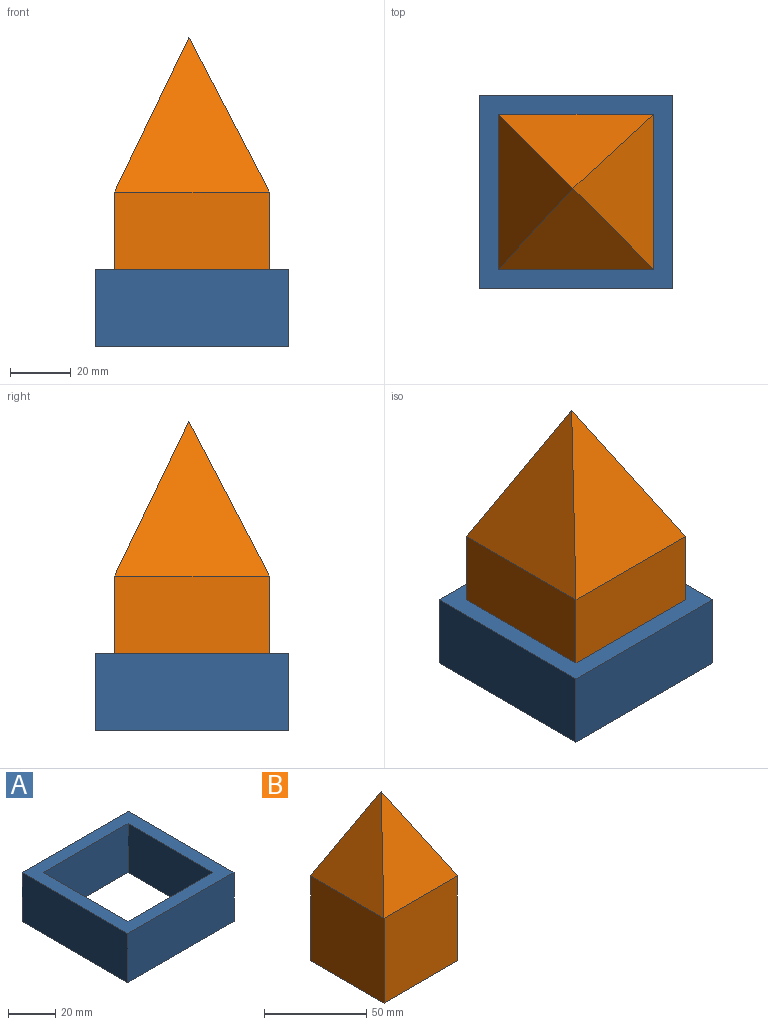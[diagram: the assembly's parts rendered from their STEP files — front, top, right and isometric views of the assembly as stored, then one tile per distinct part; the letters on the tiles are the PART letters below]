
ASSEMBLY  parts=2 mates=1
PART A: 10 faces, bbox 63.5x63.5x25.4 mm
  f0: plane 63.5x25.4mm, normal (0,-1,0), area 1612.9mm2, adj f1,f7,f8,f9
  f1: plane 63.5x25.4mm, normal (1,0,0), area 1612.9mm2, adj f0,f2,f8,f9
  f2: plane 63.5x25.4mm, normal (0,1,0), area 1612.9mm2, adj f1,f7,f8,f9
  f3: plane 50.8x25.4mm, normal (-1,0,0), area 1290.3mm2, adj f4,f6,f8,f9
  f4: plane 50.8x25.4mm, normal (0,1,0), area 1290.3mm2, adj f3,f5,f8,f9
  f5: plane 50.8x25.4mm, normal (1,0,0), area 1290.3mm2, adj f4,f6,f8,f9
  f6: plane 50.8x25.4mm, normal (0,-1,0), area 1290.3mm2, adj f3,f5,f8,f9
  f7: plane 63.5x25.4mm, normal (-1,0,0), area 1612.9mm2, adj f0,f2,f8,f9
  f8: plane 63.5x63.5mm, normal (0,0,1), area 1451.6mm2, adj f0,f1,f2,f3,f4,f5,f6,f7
  f9: plane 63.5x63.5mm, normal (0,0,-1), area 1451.6mm2, adj f0,f1,f2,f3,f4,f5,f6,f7
PART B: 9 faces, bbox 50.8x50.8x101.6 mm
  f0: plane 50.8x50.8mm, normal (0,1,0), area 2580.6mm2, adj f1,f3,f4,f8
  f1: plane 50.8x50.8mm, normal (-1,0,0), area 2580.6mm2, adj f0,f2,f4,f5
  f2: plane 50.8x50.8mm, normal (0,-1,0), area 2580.6mm2, adj f1,f3,f4,f6
  f3: plane 50.8x50.8mm, normal (1,0,0), area 2580.6mm2, adj f0,f2,f4,f7
  f4: plane 50.8x50.8mm, normal (0,0,-1), area 2580.6mm2, adj f0,f1,f2,f3
  f5: plane 50.8x50.8mm, normal (-0.9,0,0.43), area 1431.5mm2, adj f1,f6,f8
  f6: plane 50.8x50.8mm, normal (0,-0.89,0.46), area 1454.6mm2, adj f2,f5,f7
  f7: plane 50.8x50.8mm, normal (0.89,0,0.46), area 1454.1mm2, adj f3,f6,f8
  f8: plane 50.8x50.8mm, normal (0,0.9,0.43), area 1431.1mm2, adj f0,f5,f7
PLACE A at identity fixed
PLACE B t=(64.61,66.52,0)mm
MATE slider B.f4 <-> A.f9  axis (0,0,-1) through (13.81,15.72,0)mm
